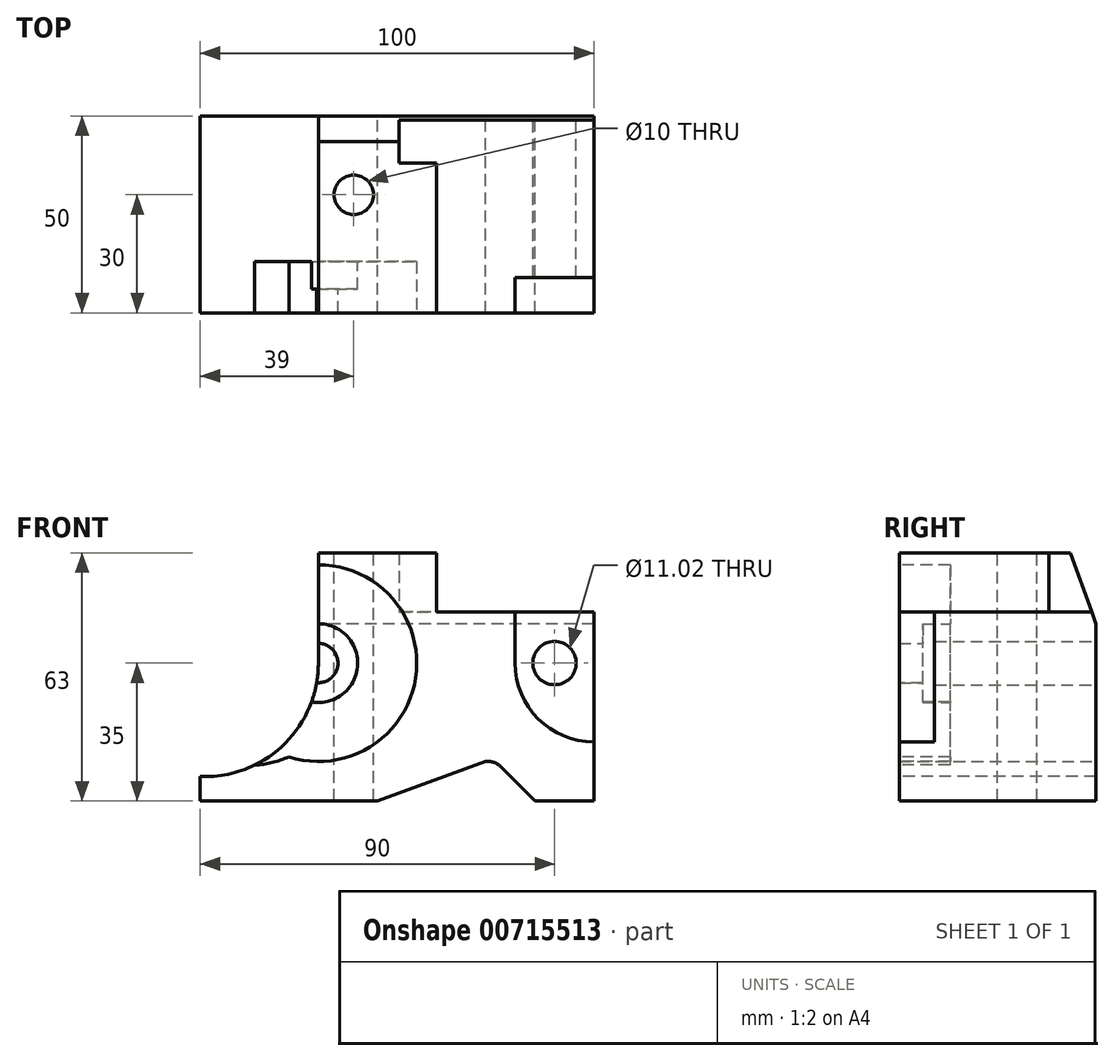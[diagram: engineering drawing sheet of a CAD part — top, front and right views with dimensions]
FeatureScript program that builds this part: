
annotation { "Feature Type Name" : "Feature", "Feature Type Description" : "" }
export const myFeature = defineFeature(function(context is Context, id is Id, definition is map)
    precondition{}
    {
        {
            var Q0;
            Q0=qCreatedBy(makeId("Front.planeOp"),FACE);
            var sketch = newSketch(context, id + "F0", { "sketchPlane" : qUnion([Q0])});
            skLineSegment(sketch, "E0", {"start": v(60, 0) * mm, "end": v(60, -15) * mm});
            skLineSegment(sketch, "E1", {"start": v(60, -15) * mm, "end": v(100, -15) * mm});
            skLineSegment(sketch, "E2", {"start": v(60, 0) * mm, "end": v(0, 0) * mm});
            skLineSegment(sketch, "E3", {"start": v(0, 0) * mm, "end": v(0, -63) * mm});
            skLineSegment(sketch, "E4", {"start": v(0, -63) * mm, "end": v(45, -63) * mm});
            skLineSegment(sketch, "E5", {"start": v(45, -63) * mm, "end": v(72.46, -53) * mm});
            skLineSegment(sketch, "E6", {"start": v(100, -63) * mm, "end": v(100, -15) * mm});
            skLineSegment(sketch, "E7", {"start": v(100, -63) * mm, "end": v(85, -63) * mm});
            skLineSegment(sketch, "E8", {"start": v(76.27, -54.27) * mm, "end": v(85, -63) * mm});
            skPoint(sketch, "E9.visualSharp", {"position": v(74.33, -52.33) * mm});
            skArc(sketch, "E10", {"start": v(76.27, -54.27) * mm, "mid": v(74.51, -53.18) * mm, "end": v(72.46, -53) * mm});
            skCircle(sketch, "E11", {"center": v(90, -28) * mm, "radius": 5.51 * mm});
            skSolve(sketch);
        }
        {
            var Q0;
            Q0 = qSketchRegion(id + "F0", true);
            extrude(context, id + "F1", {"entities" : qUnion([Q0]), "depth" : 50 * mm, "offsetDistance" : 25.4 * mm});
        }
        {
            var Q0;
            Q0=makeQuery(id+"F1.opExtrude","CAP_FACE",FACE,{"disambiguationData":[OSD([sQuery(id+"F0.wireOp",EDGE,"E0"),sQuery(id+"F0.wireOp",EDGE,"E1"),sQuery(id+"F0.wireOp",EDGE,"E2"),sQuery(id+"F0.wireOp",EDGE,"E3"),sQuery(id+"F0.wireOp",EDGE,"E4"),sQuery(id+"F0.wireOp",EDGE,"E5"),sQuery(id+"F0.wireOp",EDGE,"E6"),sQuery(id+"F0.wireOp",EDGE,"E7"),sQuery(id+"F0.wireOp",EDGE,"E8"),sQuery(id+"F0.wireOp",EDGE,"E10"),sQuery(id+"F0.wireOp",EDGE,"E11")])],"isStart":false});
            var sketch = newSketch(context, id + "F2", { "sketchPlane" : qUnion([Q0])});
            skLineSegment(sketch, "E12", {"start": v(0, 0) * mm, "end": v(30, 0) * mm});
            skLineSegment(sketch, "E13", {"start": v(30, 0) * mm, "end": v(30, -3) * mm});
            skArc(sketch, "E14", {"start": v(22.5, -51.85) * mm, "mid": v(54.71, -31.8) * mm, "end": v(30, -3) * mm});
            skPoint(sketch, "E14.second.point", {"position": v(38.78, -51.4) * mm});
            skPoint(sketch, "E14.third.point", {"position": v(30, -53) * mm});
            skArc(sketch, "E15", {"start": v(0, -50.62) * mm, "mid": v(11.1, -53.92) * mm, "end": v(22.5, -51.85) * mm});
            skPoint(sketch, "E15.first.point", {"position": v(0, -50.62) * mm});
            skPoint(sketch, "E15.second.point", {"position": v(22.5, -51.85) * mm});
            skPoint(sketch, "E15.second.point.positionSnap0", {"position": v(22.5, -63) * mm});
            skPoint(sketch, "E15.third.point", {"position": v(0, -7.28) * mm});
            skSolve(sketch);
        }
        {
            var Q0;
            {var subQ1=sQuery(id+"F2.wireOp",EDGE,"E12");Q0=makeQuery(id+"F2.imprint","IMPRINT",FACE,{"disambiguationData":[TD([[makeQuery(id+"F2.imprint","IMPRINT",EDGE,{"derivedFrom":subQ1}),1.0]])]});}
            extrude(context, id + "F3", {"entities" : qUnion([Q0]), "operationType" : NewBodyOperationType.REMOVE, "oppositeDirection" : true, "depth" : 13 * mm, "offsetDistance" : 25.4 * mm});
        }
        {
            var Q0;
            Q0=makeQuery(id+"F3.boolean.opBoolean","COPY",FACE,{"derivedFrom":makeQuery(id+"F3.opExtrude","CAP_FACE",FACE,{"disambiguationData":[OSD([sQuery(id+"F0.wireOp",EDGE,"E3"),sQuery(id+"F2.wireOp",EDGE,"E12"),sQuery(id+"F2.wireOp",EDGE,"E13"),sQuery(id+"F2.wireOp",EDGE,"E14"),sQuery(id+"F2.wireOp",EDGE,"E15")])],"isStart":false})});
            var sketch = newSketch(context, id + "F4", { "sketchPlane" : qUnion([Q0])});
            skCircle(sketch, "E16", {"center": v(30, -28) * mm, "radius": 10 * mm});
            skSolve(sketch);
        }
        {
            var Q0;
            Q0 = qSketchRegion(id + "F4", true);
            extrude(context, id + "F5", {"entities" : qUnion([Q0]), "operationType" : NewBodyOperationType.ADD, "depth" : 7 * mm, "offsetDistance" : 25.4 * mm});
        }
        {
            var Q0;
            Q0=makeQuery(id+"F5.opExtrude","CAP_FACE",FACE,{"disambiguationData":[OSD([sQuery(id+"F4.wireOp",EDGE,"E16")])],"isStart":false});
            var sketch = newSketch(context, id + "F6", { "sketchPlane" : qUnion([Q0])});
            skCircle(sketch, "E17", {"center": v(30, -28) * mm, "radius": 5 * mm});
            skSolve(sketch);
        }
        {
            var Q0;
            Q0 = qSketchRegion(id + "F6", true);
            extrude(context, id + "F7", {"entities" : qUnion([Q0]), "operationType" : NewBodyOperationType.ADD, "depth" : 6 * mm, "offsetDistance" : 25.4 * mm});
        }
        {
            var Q0;
            Q0=makeQuery(id+"F1.opExtrude","CAP_FACE",FACE,{"disambiguationData":[OSD([sQuery(id+"F0.wireOp",EDGE,"E0"),sQuery(id+"F0.wireOp",EDGE,"E1"),sQuery(id+"F0.wireOp",EDGE,"E2"),sQuery(id+"F0.wireOp",EDGE,"E3"),sQuery(id+"F0.wireOp",EDGE,"E4"),sQuery(id+"F0.wireOp",EDGE,"E5"),sQuery(id+"F0.wireOp",EDGE,"E6"),sQuery(id+"F0.wireOp",EDGE,"E7"),sQuery(id+"F0.wireOp",EDGE,"E8"),sQuery(id+"F0.wireOp",EDGE,"E10"),sQuery(id+"F0.wireOp",EDGE,"E11")])],"isStart":false});
            var sketch = newSketch(context, id + "F8", { "sketchPlane" : qUnion([Q0])});
            skLineSegment(sketch, "E18", {"start": v(80, -15) * mm, "end": v(80, -28) * mm});
            skArc(sketch, "E19", {"start": v(80, -28) * mm, "mid": v(85.86, -42.14) * mm, "end": v(100, -48) * mm});
            skSolve(sketch);
        }
        {
            var Q0;
            {var subQ4=sQuery(id+"F8.wireOp",EDGE,"E18");Q0=makeQuery(id+"F8.imprint","IMPRINT",FACE,{"disambiguationData":[TD([[makeQuery(id+"F8.imprint","IMPRINT",EDGE,{"derivedFrom":subQ4}),1.0]])]});}
            extrude(context, id + "F9", {"entities" : qUnion([Q0]), "operationType" : NewBodyOperationType.REMOVE, "oppositeDirection" : true, "depth" : 9 * mm, "offsetDistance" : 25.4 * mm});
        }
        {
            var Q0;
            Q0=makeQuery(id+"F1.opExtrude","CAP_FACE",FACE,{"disambiguationData":[OSD([sQuery(id+"F0.wireOp",EDGE,"E0"),sQuery(id+"F0.wireOp",EDGE,"E1"),sQuery(id+"F0.wireOp",EDGE,"E2"),sQuery(id+"F0.wireOp",EDGE,"E3"),sQuery(id+"F0.wireOp",EDGE,"E4"),sQuery(id+"F0.wireOp",EDGE,"E5"),sQuery(id+"F0.wireOp",EDGE,"E6"),sQuery(id+"F0.wireOp",EDGE,"E7"),sQuery(id+"F0.wireOp",EDGE,"E8"),sQuery(id+"F0.wireOp",EDGE,"E10"),sQuery(id+"F0.wireOp",EDGE,"E11")])],"isStart":false});
            var sketch = newSketch(context, id + "F10", { "sketchPlane" : qUnion([Q0])});
            skLineSegment(sketch, "E20", {"start": v(0, 0) * mm, "end": v(30, 0) * mm});
            skLineSegment(sketch, "E21", {"start": v(30, 0) * mm, "end": v(30, -28) * mm});
            skArc(sketch, "E22", {"start": v(30, -28) * mm, "mid": v(21.14, -48.8) * mm, "end": v(0, -56.81) * mm});
            skLineSegment(sketch, "E23", {"start": v(0, 0) * mm, "end": v(0, -56.81) * mm});
            skSolve(sketch);
        }
        {
            var Q0;
            Q0 = qSketchRegion(id + "F10", true);
            extrude(context, id + "F11", {"entities" : qUnion([Q0]), "operationType" : NewBodyOperationType.REMOVE, "oppositeDirection" : true, "depth" : 381 * mm, "offsetDistance" : 25.4 * mm});
        }
        {
            var Q0;
            Q0=makeQuery(id+"F11.boolean.opBoolean","MERGE",FACE,{"derivedFrom":[makeQuery(id+"F3.boolean.opBoolean","COPY",FACE,{"derivedFrom":makeQuery(id+"F3.opExtrude","SWEPT_FACE",FACE,{"disambiguationData":[OSD([sQuery(id+"F2.wireOp",EDGE,"E13")])]})}),makeQuery(id+"F11.opExtrude","SWEPT_FACE",FACE,{"disambiguationData":[OSD([sQuery(id+"F10.wireOp",EDGE,"E21")])]})]});
            var sketch = newSketch(context, id + "F12", { "sketchPlane" : qUnion([Q0])});
            skLineSegment(sketch, "E24", {"start": v(0, 0) * mm, "end": v(6.55, 0) * mm});
            skLineSegment(sketch, "E25", {"start": v(6.55, 0) * mm, "end": v(0, -18) * mm});
            skLineSegment(sketch, "E26", {"start": v(0, -18) * mm, "end": v(0, 0) * mm});
            skSolve(sketch);
        }
        {
            var Q0;
            Q0 = qSketchRegion(id + "F12", true);
            extrude(context, id + "F13", {"entities" : qUnion([Q0]), "operationType" : NewBodyOperationType.REMOVE, "oppositeDirection" : true, "depth" : 381 * mm, "offsetDistance" : 25.4 * mm});
        }
        {
            var Q0;
            Q0=qCreatedBy(makeId("Top.planeOp"),FACE);
            var sketch = newSketch(context, id + "F14", { "sketchPlane" : qUnion([Q0])});
            skLineSegment(sketch, "E27.bottom", {"start": v(50.51, -12) * mm, "end": v(100.51, -12) * mm});
            skLineSegment(sketch, "E27.top", {"start": v(50.51, 0) * mm, "end": v(100.51, 0) * mm});
            skLineSegment(sketch, "E27.left", {"start": v(50.51, -12) * mm, "end": v(50.51, 0) * mm});
            skLineSegment(sketch, "E27.right", {"start": v(100.51, -12) * mm, "end": v(100.51, 0) * mm});
            skSolve(sketch);
        }
        {
            var Q0;
            Q0 = qSketchRegion(id + "F14", true);
            extrude(context, id + "F15", {"entities" : qUnion([Q0]), "operationType" : NewBodyOperationType.REMOVE, "oppositeDirection" : true, "depth" : 15 * mm, "offsetDistance" : 25.4 * mm});
        }
        {
            var Q0;
            Q0=makeQuery(id+"F1.opExtrude","SWEPT_FACE",FACE,{"disambiguationData":[OSD([sQuery(id+"F0.wireOp",EDGE,"E2")])]});
            var sketch = newSketch(context, id + "F16", { "sketchPlane" : qUnion([Q0])});
            skCircle(sketch, "E28", {"center": v(39, -20) * mm, "radius": 5 * mm});
            skSolve(sketch);
        }
        {
            var Q0;
            Q0 = qSketchRegion(id + "F16", true);
            extrude(context, id + "F17", {"entities" : qUnion([Q0]), "operationType" : NewBodyOperationType.REMOVE, "oppositeDirection" : true, "depth" : 381 * mm, "offsetDistance" : 25.4 * mm});
        }
    });
